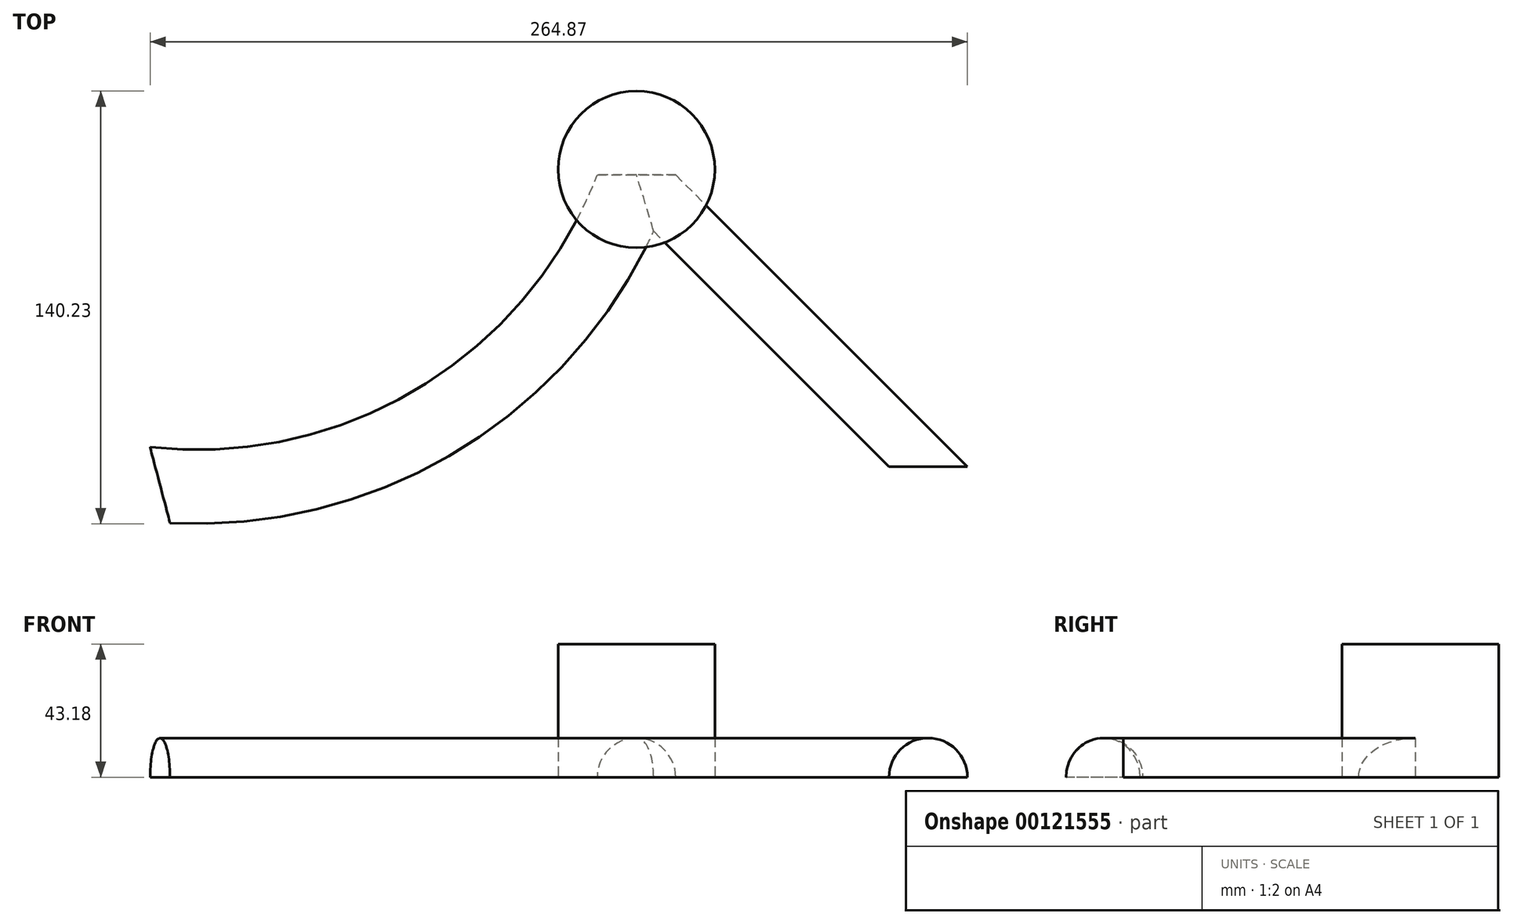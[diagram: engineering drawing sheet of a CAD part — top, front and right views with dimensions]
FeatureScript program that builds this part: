
annotation { "Feature Type Name" : "Feature", "Feature Type Description" : "" }
export const myFeature = defineFeature(function(context is Context, id is Id, definition is map)
    precondition{}
    {
        {
            var Q0;
            Q0=qCreatedBy(makeId("Top.planeOp"),FACE);
            var sketch = newSketch(context, id + "F0", { "sketchPlane" : qUnion([Q0])});
            skCircle(sketch, "E0", {"center": v(0, 0) * mm, "radius": 25.4 * mm});
            skSolve(sketch);
        }
        {
            var Q0;
            Q0=makeQuery(id+"F0.imprint","IMPRINT",FACE,{"disambiguationData":[TD([[makeQuery(id+"F0.imprint","IMPRINT",EDGE,{"derivedFrom":sQuery(id+"F0.wireOp",EDGE,"E0")}),1.0]])]});
            extrude(context, id + "F1", {"entities" : qUnion([Q0]), "depth" : 43.18 * mm});
        }
        {
            var Q0;
            Q0=makeQuery(id+"F1.opExtrude","SWEPT_BODY",BODY,{"disambiguationData":[OSD([sQuery(id+"F0.wireOp",EDGE,"E0")])]});
            var Q1;
            Q1=qCreatedBy(makeId("Front.planeOp"),FACE);
            transform(context, id + "F2", {"entities" : qUnion([Q0]), "transformType" : TransformType.TRANSLATION_DISTANCE, "transformDirection" : qUnion([Q1]), "distance" : 74.9 * mm, "makeCopy" : false});
        }
        {
            var Q0;
            Q0=qCreatedBy(makeId("Front.planeOp"),FACE);
            var sketch = newSketch(context, id + "F3", { "sketchPlane" : qUnion([Q0])});
            skCircle(sketch, "E1", {"center": v(0, 0) * mm, "radius": 12.7 * mm});
            skLineSegment(sketch, "E2", {"start": v(-12.7, 0) * mm, "end": v(12.7, 0) * mm});
            skSolve(sketch);
        }
        {
            var Q0;
            Q0=qCreatedBy(makeId("Top.planeOp"),FACE);
            var sketch = newSketch(context, id + "F4", { "sketchPlane" : qUnion([Q0])});
            skArc(sketch, "E3", {"start": v(-154.37, -100.57) * mm, "mid": v(-60.04, -76.6) * mm, "end": v(0, 0) * mm});
            skSolve(sketch);
        }
        {
            var Q0;
            {var subQ0=sQuery(id+"F3.wireOp",EDGE,"E2");Q0=makeQuery(id+"F3.imprint","IMPRINT",FACE,{"disambiguationData":[TD([[makeQuery(id+"F3.imprint","IMPRINT",EDGE,{"derivedFrom":subQ0}),1.0]])]});}
            var Q1;
            Q1=sQuery(id+"F4.wireOp",EDGE,"E3");
            sweep(context, id + "F5", {"profiles" : qUnion([Q0]), "path" : qUnion([Q1])});
        }
        {
            var Q0;
            Q0=qCreatedBy(makeId("Top.planeOp"),FACE);
            var sketch = newSketch(context, id + "F6", { "sketchPlane" : qUnion([Q0])});
            skLineSegment(sketch, "E4", {"start": v(0, 0) * mm, "end": v(94.57, -94.57) * mm});
            skLineSegment(sketch, "E5", {"start": v(0, -94.63) * mm, "end": v(0, 0) * mm});
            skSolve(sketch);
        }
        {
            var Q0;
            Q0=makeQuery(id+"F5.opSweep","CAP_FACE",FACE,{"disambiguationData":[OSD([sQuery(id+"F3.wireOp",EDGE,"E1"),sQuery(id+"F3.wireOp",EDGE,"E2"),sQuery(id+"F4.wireOp",VERTEX,"E3.end")])],"isStart":true});
            var Q1;
            Q1=sQuery(id+"F6.wireOp",EDGE,"E4");
            sweep(context, id + "F7", {"operationType" : NewBodyOperationType.ADD, "profiles" : qUnion([Q0]), "path" : qUnion([Q1])});
        }
        {
            var Q0;
            Q0=makeQuery(id+"F1.opExtrude","SWEPT_BODY",BODY,{"disambiguationData":[OSD([sQuery(id+"F0.wireOp",EDGE,"E0")])]});
            var Q1;
            Q1=qCreatedBy(makeId("Front.planeOp"),FACE);
            transform(context, id + "F8", {"entities" : qUnion([Q0]), "transformType" : TransformType.TRANSLATION_DISTANCE, "transformDirection" : qUnion([Q1]), "distance" : 76.65 * mm, "oppositeDirection" : true, "makeCopy" : false});
        }
    });
